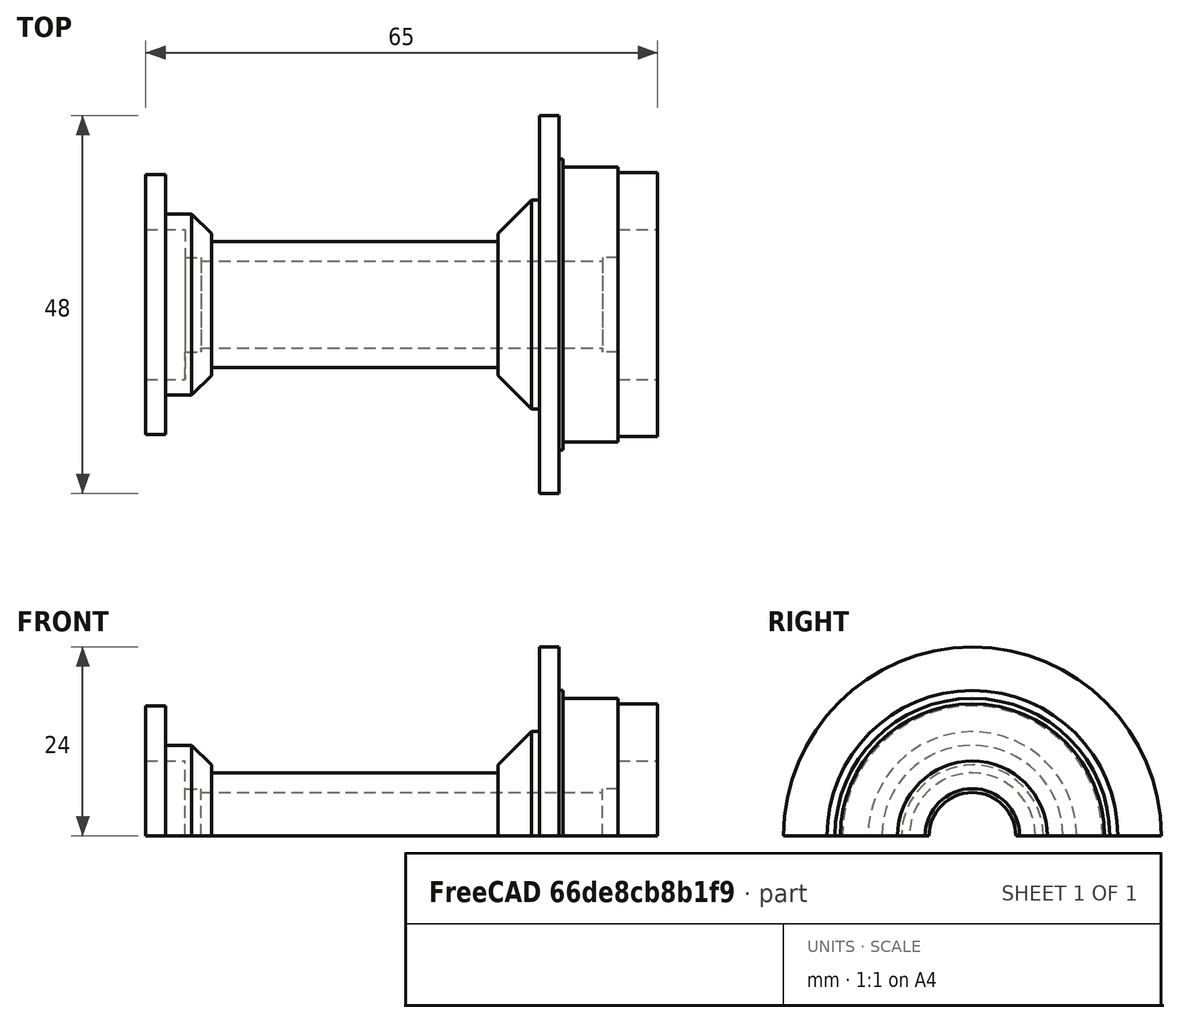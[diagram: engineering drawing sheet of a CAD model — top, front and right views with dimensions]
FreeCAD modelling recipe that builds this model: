
FCSTD DOCUMENT  (FreeCAD 0.16R)
Label: 75mmFixie
License: All rights reserved
LicenseURL: http://en.wikipedia.org/wiki/All_rights_reserved
objects: Sketcher::SketchObject×1, PartDesign::Revolution×1, Mesh::Feature×1
note: 3 computed .brp shape members not serialized (recipe doc carries the construction recipe); baked Part::Feature solids carry a one-line shape summary decoded from their .brp

FEATURE [Sketcher::SketchObject] Sketch
  sketch-geometry (28):
    g0: LineSegment StartX=-5 StartY=6 StartZ=0 EndX=-5 EndY=9.5 EndZ=0
    g1: LineSegment StartX=-5 StartY=9.5 StartZ=0 EndX=0 EndY=9.5 EndZ=0
    g2: LineSegment StartX=0 StartY=9.5 StartZ=0 EndX=0 EndY=16.76 EndZ=0
    g3: LineSegment StartX=0 StartY=16.76 StartZ=0 EndX=-5 EndY=16.76 EndZ=0
    g4: LineSegment StartX=-5 StartY=16.76 StartZ=0 EndX=-5 EndY=17.46 EndZ=0
    g5: LineSegment StartX=-5 StartY=17.46 StartZ=0 EndX=-12 EndY=17.46 EndZ=0
    g6: LineSegment StartX=-12 StartY=17.46 StartZ=0 EndX=-12 EndY=18.46 EndZ=0
    g7: LineSegment StartX=-12 StartY=18.46 StartZ=0 EndX=-12.5 EndY=18.46 EndZ=0
    g8: LineSegment StartX=-12.5 StartY=18.46 StartZ=0 EndX=-12.5 EndY=24 EndZ=0
    g9: LineSegment StartX=-12.5 StartY=24 StartZ=0 EndX=-15 EndY=24 EndZ=0
    g10: LineSegment StartX=-15 StartY=24 StartZ=0 EndX=-15 EndY=13.2426 EndZ=0
    g11: LineSegment StartX=-15 StartY=13.2426 StartZ=0 EndX=-16 EndY=13.2426 EndZ=0
    g12: LineSegment StartX=-16 StartY=13.2426 StartZ=0 EndX=-20.2426 EndY=9 EndZ=0
    g13: LineSegment StartX=-20.2426 StartY=9 StartZ=0 EndX=-20.2426 EndY=8 EndZ=0
    g14: LineSegment StartX=-20.2426 StartY=8 StartZ=0 EndX=-56.6716 EndY=8 EndZ=0
    g15: LineSegment StartX=-56.6716 StartY=8 StartZ=0 EndX=-56.6716 EndY=9 EndZ=0
    g16: LineSegment StartX=-56.6716 StartY=9 StartZ=0 EndX=-59.1716 EndY=11.5 EndZ=0
    g17: LineSegment StartX=-59.1716 StartY=11.5 StartZ=0 EndX=-62.5 EndY=11.5 EndZ=0
    g18: LineSegment StartX=-62.5 StartY=11.5 StartZ=0 EndX=-62.5 EndY=16.5 EndZ=0
    g19: LineSegment StartX=-62.5 StartY=16.5 StartZ=0 EndX=-65 EndY=16.5 EndZ=0
    g20: LineSegment StartX=-65 StartY=16.5 StartZ=0 EndX=-65 EndY=9.5 EndZ=0
    g21: LineSegment StartX=-65 StartY=9.5 StartZ=0 EndX=-60 EndY=9.5 EndZ=0
    g22: LineSegment StartX=-60 StartY=9.5 StartZ=0 EndX=-60 EndY=6 EndZ=0
    g23: LineSegment StartX=-60 StartY=6 StartZ=0 EndX=-58 EndY=6 EndZ=0
    g24: LineSegment StartX=-58 StartY=6 StartZ=0 EndX=-58 EndY=5.5 EndZ=0
    g25: LineSegment StartX=-58 StartY=5.5 StartZ=0 EndX=-7 EndY=5.5 EndZ=0
    g26: LineSegment StartX=-5 StartY=6 StartZ=0 EndX=-7 EndY=6 EndZ=0
    g27: LineSegment StartX=-7 StartY=6 StartZ=0 EndX=-7 EndY=5.5 EndZ=0
  constraints (84):
    c: Coincident(g0,g1)
    c: Horizontal(g1)
    c: Coincident(g1,g2)
    c: Coincident(g2,g3)
    c: Horizontal(g3)
    c: Coincident(g3,g4)
    c: Coincident(g4,g5)
    c: Coincident(g5,g6)
    c: Coincident(g6,g7)
    c: Coincident(g7,g8)
    c: Vertical(g8)
    c: Coincident(g8,g9)
    c: Horizontal(g9)
    c: Coincident(g9,g10)
    c: Vertical(g10)
    c: Coincident(g10,g11)
    c: Coincident(g11,g12)
    c: Coincident(g12,g13)
    c: Vertical(g13)
    c: Coincident(g13,g14)
    c: Horizontal(g14)
    c: Coincident(g14,g15)
    c: Vertical(g15)
    c: Coincident(g15,g16)
    c: Coincident(g16,g17)
    c: Horizontal(g17)
    c: Coincident(g17,g18)
    c: Vertical(g18)
    c: Coincident(g18,g19)
    c: Coincident(g19,g20)
    c: Vertical(g20)
    c: Coincident(g20,g21)
    c: Coincident(g21,g22)
    c: Vertical(g22)
    c: Coincident(g22,g23)
    c: Horizontal(g23)
    c: Coincident(g23,g24)
    c: Coincident(g24,g25)
    c: Horizontal(g25)
    c: Coincident(g26,g0)
    c: Coincident(g27,g26)
    c: Coincident(g27,g25)
    c: Equal(g24,g27)
    c: Vertical(g27)
    c: Vertical(g24)
    c: Horizontal(g26)
    c: Horizontal(g11)
    c: Horizontal(g5)
    c: Horizontal(g19)
    c: Horizontal(g21)
    c: DistanceY(g-1,g0) = 6
    c: DistanceY(g-1,g25) = 5.5
    c: DistanceY(g-1,g1) = 9.5
    c: DistanceX(g1,g1) = 5
    c: DistanceX(g21,g21) = 5
    c: DistanceY(g-1,g20) = 9.5
    c: DistanceX(g20,g1) = 65
    c: Vertical(g0)
    c: DistanceX(g23,g23) = 2
    c: DistanceX(g26,g26) = 2
    c: Vertical(g2)
    c: DistanceX(g7,g7) = 0.5
    c: Horizontal(g7)
    c: Vertical(g6)
    c: DistanceY(g-1,g4) = 17.46
    c: Vertical(g4)
    c: DistanceX(g9,g9) = 2.5
    c: DistanceY(g-1,g2) = 16.76
    c: DistanceX(g5,g5) = 7
    c: DistanceX(g3,g3) = 5
    c: DistanceY(g6,g6) = 1
    c: DistanceY(g-1,g13) = 8
    c: DistanceX(g19,g19) = 2.5
    c: DistanceY(g-1,g9) = 24
    c: Distance(g13) = 1
    c: Distance(g11) = 1
    c: Angle(g16) = 2.35619
    c: Angle(g12) = -2.35619
    c: Distance(g12) = 6
    c: DistanceX(g-1,g1) = 0
    c: DistanceY(g18,g18) = 5
    c: DistanceY(g21,g17) = 2
    c: Distance(g21,g16) = 2
    c: Distance(g15) = 1
FEATURE [PartDesign::Revolution] Revolution
  Angle = 180
  Axis = (1,0,0)
  Base = (0,0,0)
  ReferenceAxis = -> Sketch [H_Axis]
  Sketch = -> Sketch
FEATURE [Mesh::Feature] Mesh  label="Revolution (Meshed)"
